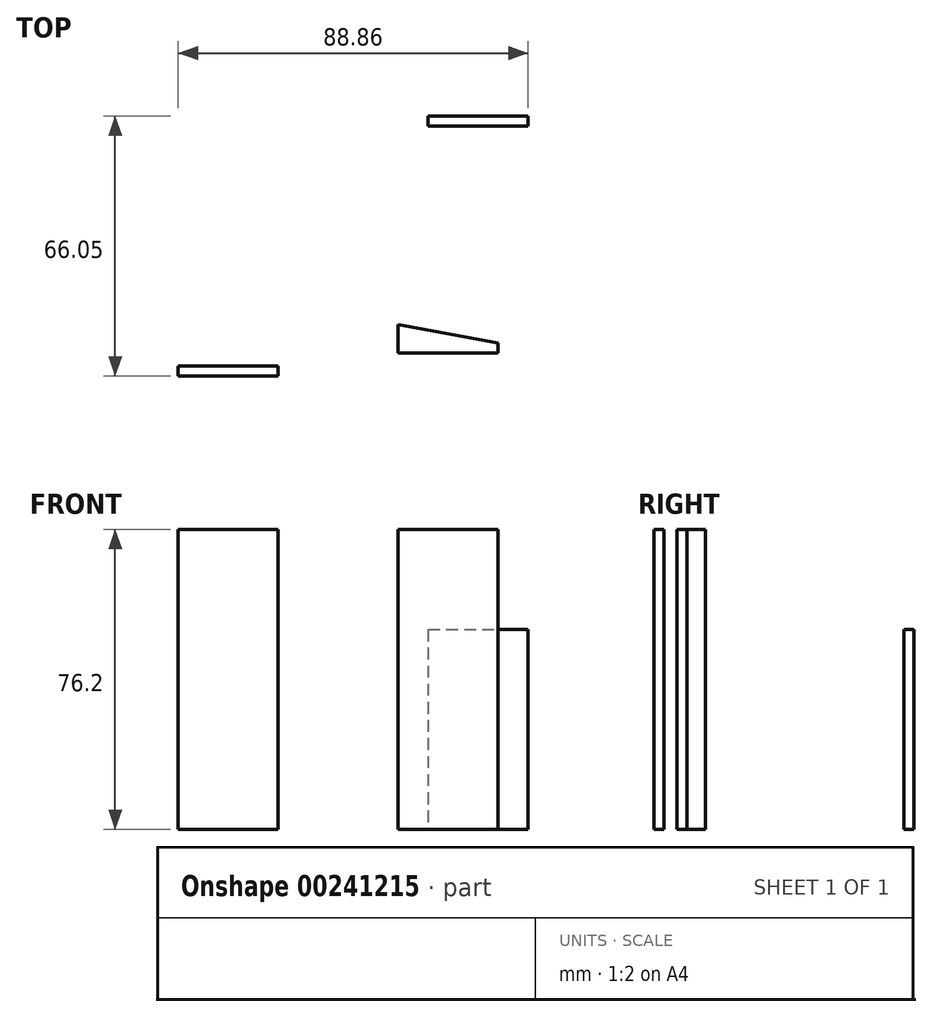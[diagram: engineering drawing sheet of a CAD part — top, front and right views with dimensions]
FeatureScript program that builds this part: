
annotation { "Feature Type Name" : "Feature", "Feature Type Description" : "" }
export const myFeature = defineFeature(function(context is Context, id is Id, definition is map)
    precondition{}
    {
        {
            var Q0;
            Q0=qCreatedBy(makeId("Top.planeOp"),FACE);
            var sketch = newSketch(context, id + "F0", { "sketchPlane" : qUnion([Q0])});
            skLineSegment(sketch, "E0.bottom", {"start": v(-36.13, -36.06) * mm, "end": v(-10.73, -36.06) * mm});
            skLineSegment(sketch, "E0.top", {"start": v(-36.13, -33.52) * mm, "end": v(-10.73, -33.52) * mm});
            skLineSegment(sketch, "E0.left", {"start": v(-36.13, -36.06) * mm, "end": v(-36.13, -33.52) * mm});
            skLineSegment(sketch, "E0.right", {"start": v(-10.73, -36.06) * mm, "end": v(-10.73, -33.52) * mm});
            skSolve(sketch);
        }
        {
            var Q0;
            Q0 = qSketchRegion(id + "F0", true);
            extrude(context, id + "F1", {"entities" : qUnion([Q0]), "depth" : 76.2 * mm});
        }
        {
            var Q0;
            Q0=qCreatedBy(makeId("Top.planeOp"),FACE);
            var sketch = newSketch(context, id + "F2", { "sketchPlane" : qUnion([Q0])});
            skLineSegment(sketch, "E1", {"start": v(-36.42, -23.66) * mm, "end": v(-36.42, -35.43) * mm});
            skLineSegment(sketch, "E2", {"start": v(-36.42, -35.43) * mm, "end": v(39.74, -35.43) * mm});
            skLineSegment(sketch, "E3", {"start": v(39.74, -35.43) * mm, "end": v(39.74, -23.07) * mm});
            skLineSegment(sketch, "E4", {"start": v(39.74, -23.07) * mm, "end": v(-36.42, -23.66) * mm});
            skSolve(sketch);
        }
        {
            var Q0;
            Q0=makeQuery(id+"F2.imprint","IMPRINT",FACE,{"disambiguationData":[TD([[makeQuery(id+"F2.imprint","IMPRINT",EDGE,{"derivedFrom":sQuery(id+"F2.wireOp",EDGE,"E1")}),1.0]])]});
            extrude(context, id + "F3", {"entities" : qUnion([Q0]), "operationType" : NewBodyOperationType.REMOVE, "oppositeDirection" : true, "depth" : 35.3 * mm});
        }
        {
            var Q0;
            Q0=qCreatedBy(makeId("Top.planeOp"),FACE);
            var sketch = newSketch(context, id + "F4", { "sketchPlane" : qUnion([Q0])});
            skLineSegment(sketch, "E5.bottom", {"start": v(19.64, -27.65) * mm, "end": v(45.04, -27.65) * mm});
            skLineSegment(sketch, "E5.top", {"start": v(19.64, -30.19) * mm, "end": v(45.04, -30.19) * mm});
            skLineSegment(sketch, "E5.left", {"start": v(19.64, -27.65) * mm, "end": v(19.64, -30.19) * mm});
            skLineSegment(sketch, "E5.right", {"start": v(45.04, -27.65) * mm, "end": v(45.04, -30.19) * mm});
            skLineSegment(sketch, "E6", {"start": v(45.04, -27.65) * mm, "end": v(19.64, -22.96) * mm});
            skLineSegment(sketch, "E7", {"start": v(19.64, -22.96) * mm, "end": v(19.64, -27.65) * mm});
            skSolve(sketch);
        }
        {
            var Q0;
            Q0 = qSketchRegion(id + "F4", true);
            extrude(context, id + "F5", {"entities" : qUnion([Q0]), "depth" : 76.2 * mm});
        }
        {
            var Q0;
            Q0=qCreatedBy(makeId("Top.planeOp"),FACE);
            var sketch = newSketch(context, id + "F6", { "sketchPlane" : qUnion([Q0])});
            skLineSegment(sketch, "E8.bottom", {"start": v(27.33, 29.99) * mm, "end": v(52.73, 29.99) * mm});
            skLineSegment(sketch, "E8.top", {"start": v(27.33, 27.45) * mm, "end": v(52.73, 27.45) * mm});
            skLineSegment(sketch, "E8.left", {"start": v(27.33, 29.99) * mm, "end": v(27.33, 27.45) * mm});
            skLineSegment(sketch, "E8.right", {"start": v(52.73, 29.99) * mm, "end": v(52.73, 27.45) * mm});
            skSolve(sketch);
        }
        {
            var Q0;
            Q0 = qSketchRegion(id + "F6", true);
            extrude(context, id + "F7", {"entities" : qUnion([Q0]), "depth" : 50.8 * mm});
        }
    });
